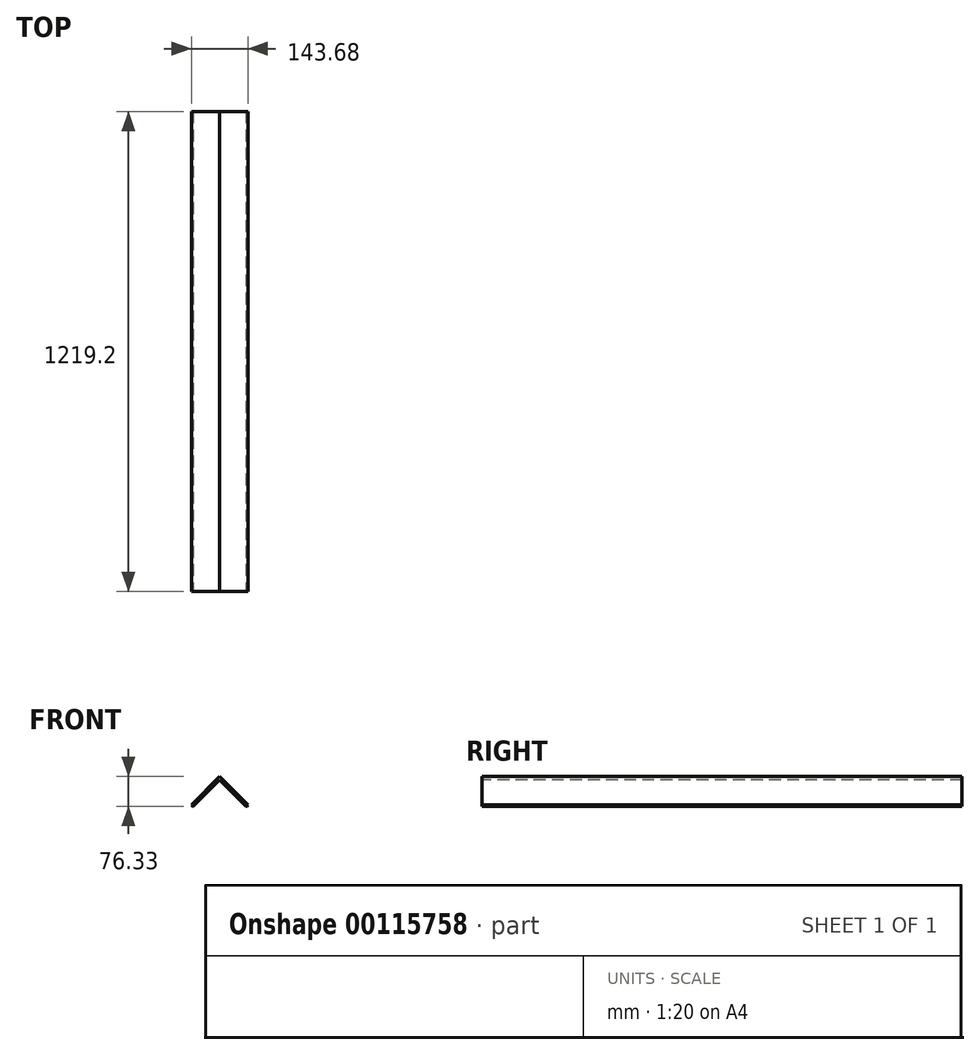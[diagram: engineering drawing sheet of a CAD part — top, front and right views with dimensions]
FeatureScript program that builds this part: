
annotation { "Feature Type Name" : "Feature", "Feature Type Description" : "" }
export const myFeature = defineFeature(function(context is Context, id is Id, definition is map)
    precondition{}
    {
        {
            var Q0;
            Q0=qCreatedBy(makeId("Front.planeOp"),FACE);
            var sketch = newSketch(context, id + "F0", { "sketchPlane" : qUnion([Q0])});
            skLineSegment(sketch, "E0", {"start": v(0, 0) * mm, "end": v(71.84, 71.84) * mm});
            skLineSegment(sketch, "E1", {"start": v(71.84, 71.84) * mm, "end": v(143.68, 0) * mm});
            skLineSegment(sketch, "E2.0", {"start": v(71.84, 62.86) * mm, "end": v(139.2, -4.5) * mm});
            skLineSegment(sketch, "E2.1", {"start": v(4.5, -4.5) * mm, "end": v(71.84, 62.86) * mm});
            skLineSegment(sketch, "E3", {"start": v(4.5, -4.5) * mm, "end": v(2.9, -4.5) * mm});
            skLineSegment(sketch, "E4", {"start": v(139.2, -4.5) * mm, "end": v(140.78, -4.5) * mm});
            skLineSegment(sketch, "E5", {"start": v(140.78, -4.5) * mm, "end": v(143.68, 0) * mm});
            skLineSegment(sketch, "E6", {"start": v(2.9, -4.5) * mm, "end": v(0, 0) * mm});
            skSolve(sketch);
        }
        {
            var Q0;
            Q0 = qSketchRegion(id + "F0", true);
            extrude(context, id + "F1", {"entities" : qUnion([Q0]), "oppositeDirection" : true, "depth" : 1219.2 * mm});
        }
    });
